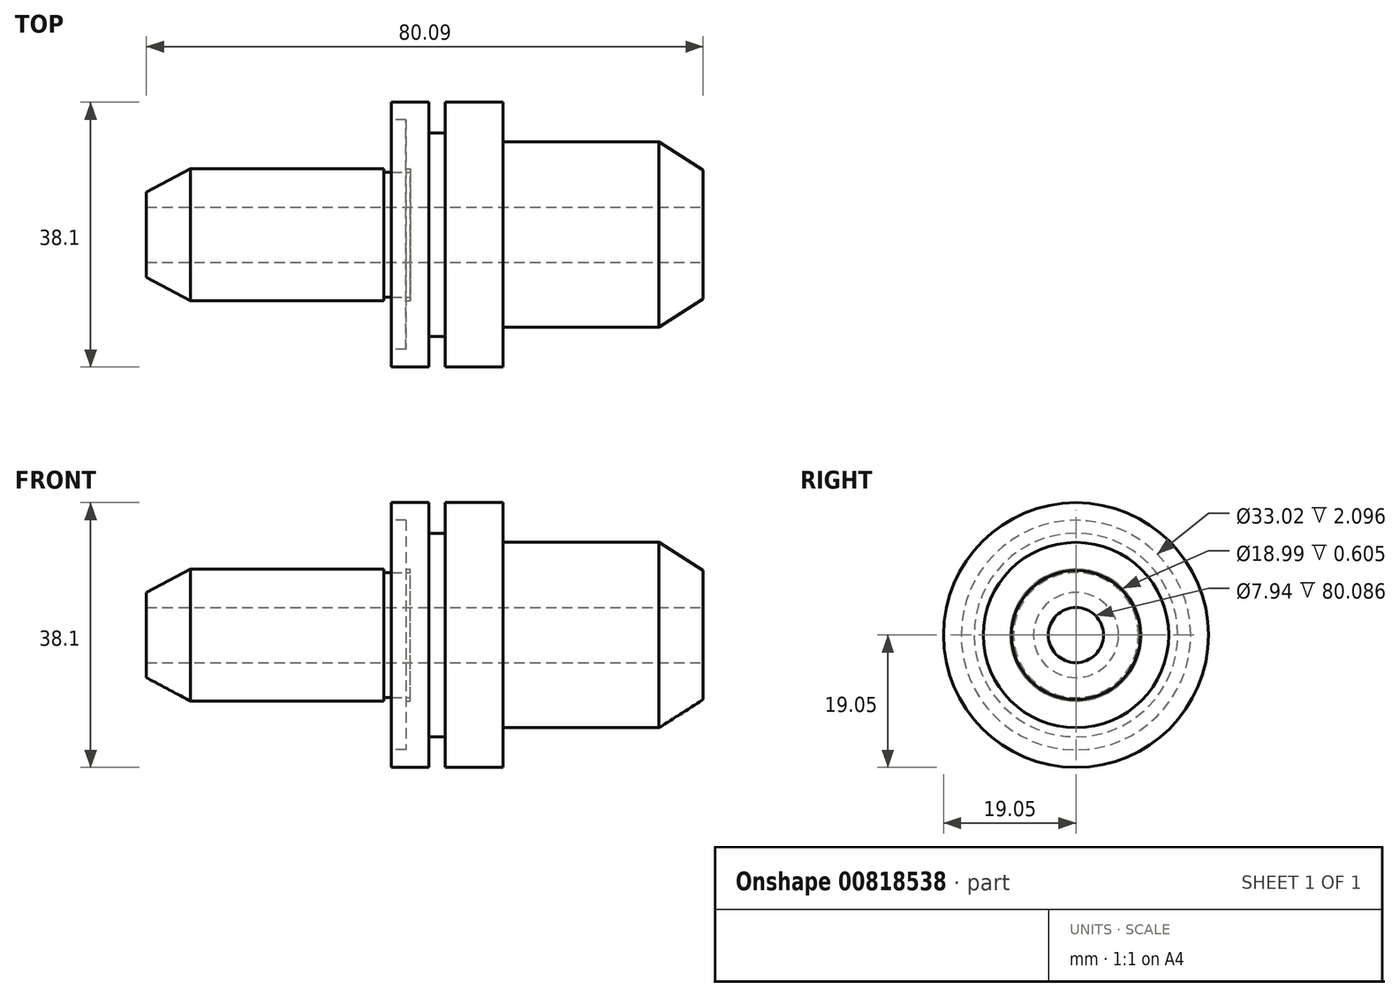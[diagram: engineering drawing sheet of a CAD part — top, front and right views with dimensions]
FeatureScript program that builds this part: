
annotation { "Feature Type Name" : "Feature", "Feature Type Description" : "" }
export const myFeature = defineFeature(function(context is Context, id is Id, definition is map)
    precondition{}
    {
        {
            var Q0;
            Q0=qCreatedBy(makeId("Right.planeOp"),FACE);
            var sketch = newSketch(context, id + "F0", { "sketchPlane" : qUnion([Q0])});
            skCircle(sketch, "E0", {"center": v(0, 0) * mm, "radius": 9.5 * mm});
            skSolve(sketch);
        }
        {
            var Q0;
            Q0 = qSketchRegion(id + "F0", true);
            extrude(context, id + "F1", {"entities" : qUnion([Q0]), "depth" : 35.24 * mm, "offsetDistance" : 25.4 * mm});
        }
        {
            var Q0;
            Q0=makeQuery(id+"F1.opExtrude","CAP_FACE",FACE,{"disambiguationData":[OSD([sQuery(id+"F0.wireOp",EDGE,"E0")])],"isStart":false});
            var sketch = newSketch(context, id + "F2", { "sketchPlane" : qUnion([Q0])});
            skCircle(sketch, "E1", {"center": v(0, 0) * mm, "radius": 19.05 * mm});
            skSolve(sketch);
        }
        {
            var Q0;
            Q0 = qSketchRegion(id + "F2", true);
            extrude(context, id + "F3", {"entities" : qUnion([Q0]), "operationType" : NewBodyOperationType.ADD, "depth" : 16.08 * mm, "offsetDistance" : 25.4 * mm});
        }
        {
            var Q0;
            Q0=makeQuery(id+"F3.opExtrude","CAP_FACE",FACE,{"disambiguationData":[OSD([sQuery(id+"F2.wireOp",EDGE,"E1")])],"isStart":false});
            var sketch = newSketch(context, id + "F4", { "sketchPlane" : qUnion([Q0])});
            skCircle(sketch, "E2", {"center": v(0, 0) * mm, "radius": 13.34 * mm});
            skSolve(sketch);
        }
        {
            var Q0;
            Q0 = qSketchRegion(id + "F4", true);
            extrude(context, id + "F5", {"entities" : qUnion([Q0]), "operationType" : NewBodyOperationType.ADD, "depth" : 28.77 * mm, "offsetDistance" : 25.4 * mm});
        }
        {
            var Q0;
            Q0=makeQuery(id+"F5.opExtrude","CAP_FACE",FACE,{"disambiguationData":[OSD([sQuery(id+"F4.wireOp",EDGE,"E2")])],"isStart":false});
            var sketch = newSketch(context, id + "F6", { "sketchPlane" : qUnion([Q0])});
            skCircle(sketch, "E3", {"center": v(0, 0) * mm, "radius": 3.97 * mm});
            skSolve(sketch);
        }
        {
            var Q0;
            Q0 = qSketchRegion(id + "F6", true);
            extrude(context, id + "F7", {"entities" : qUnion([Q0]), "operationType" : NewBodyOperationType.REMOVE, "endBound" : BoundingType.UP_TO_NEXT, "oppositeDirection" : true, "depth" : 25.4 * mm, "offsetDistance" : 25.4 * mm});
        }
        {
            var Q0;
            Q0=makeQuery(id+"F3.opExtrude","CAP_FACE",FACE,{"disambiguationData":[OSD([sQuery(id+"F2.wireOp",EDGE,"E1")])],"isStart":true});
            var sketch = newSketch(context, id + "F8", { "sketchPlane" : qUnion([Q0])});
            skCircle(sketch, "E4.0", {"center": v(0, 0) * mm, "radius": 9.5 * mm});
            skCircle(sketch, "E5.0", {"center": v(0, 0) * mm, "radius": 16.51 * mm});
            skSolve(sketch);
        }
        {
            var Q0;
            Q0 = qSketchRegion(id + "F8", true);
            extrude(context, id + "F9", {"entities" : qUnion([Q0]), "operationType" : NewBodyOperationType.REMOVE, "oppositeDirection" : true, "depth" : 2.1 * mm, "offsetDistance" : 25.4 * mm});
        }
        {
            var Q0;
            Q0=qCreatedBy(makeId("Front.planeOp"),FACE);
            var sketch = newSketch(context, id + "F10", { "sketchPlane" : qUnion([Q0])});
            skLineSegment(sketch, "E6", {"start": v(34.13, 9.5) * mm, "end": v(37.94, 9.5) * mm});
            skLineSegment(sketch, "E7.bottom", {"start": v(37.94, 9.5) * mm, "end": v(34.13, 9.5) * mm});
            skLineSegment(sketch, "E7.top", {"start": v(37.94, 8.99) * mm, "end": v(34.13, 8.99) * mm});
            skLineSegment(sketch, "E7.left", {"start": v(37.94, 9.5) * mm, "end": v(37.94, 8.99) * mm});
            skLineSegment(sketch, "E7.right", {"start": v(34.13, 9.5) * mm, "end": v(34.13, 8.99) * mm});
            skLineSegment(sketch, "E8", {"start": v(0, 0) * mm, "end": v(87.51, 0) * mm, "construction": true});
            skSolve(sketch);
        }
        {
            var Q0;
            Q0 = qSketchRegion(id + "F10", true);
            var Q1;
            Q1=sQuery(id+"F10.wireOp",EDGE,"E8");
            revolve(context, id + "F11", {"operationType" : NewBodyOperationType.REMOVE, "surfaceOperationType" : NewSurfaceOperationType.NEW, "entities" : qUnion([Q0]), "axis" : qUnion([Q1]), "revolveType" : RevolveType.FULL, "oppositeDirection" : true});
        }
        {
            var Q0;
            Q0=qCreatedBy(makeId("Front.planeOp"),FACE);
            var sketch = newSketch(context, id + "F12", { "sketchPlane" : qUnion([Q0])});
            skLineSegment(sketch, "E9", {"start": v(40.64, 19.05) * mm, "end": v(42.99, 19.05) * mm});
            skLineSegment(sketch, "E10.top", {"start": v(40.64, 14.64) * mm, "end": v(42.99, 14.64) * mm});
            skLineSegment(sketch, "E10.left", {"start": v(40.64, 19.05) * mm, "end": v(40.64, 14.64) * mm});
            skLineSegment(sketch, "E10.right", {"start": v(42.99, 19.05) * mm, "end": v(42.99, 14.64) * mm});
            skLineSegment(sketch, "E11", {"start": v(0, 0) * mm, "end": v(85.99, 0) * mm, "construction": true});
            skSolve(sketch);
        }
        {
            var Q0;
            Q0 = qSketchRegion(id + "F12", true);
            var Q1;
            Q1=sQuery(id+"F12.wireOp",EDGE,"E11");
            revolve(context, id + "F13", {"operationType" : NewBodyOperationType.REMOVE, "surfaceOperationType" : NewSurfaceOperationType.NEW, "entities" : qUnion([Q0]), "axis" : qUnion([Q1]), "revolveType" : RevolveType.FULL, "oppositeDirection" : true});
        }
        {
            var Q0;
            Q0=qCreatedBy(makeId("Front.planeOp"),FACE);
            var sketch = newSketch(context, id + "F14", { "sketchPlane" : qUnion([Q0])});
            skLineSegment(sketch, "E12", {"start": v(0, 9.5) * mm, "end": v(6.35, 9.5) * mm});
            skLineSegment(sketch, "E13", {"start": v(73.74, 13.34) * mm, "end": v(80.09, 13.34) * mm});
            skLineSegment(sketch, "E14", {"start": v(0, 9.5) * mm, "end": v(0, 6.13) * mm});
            skLineSegment(sketch, "E15", {"start": v(0, 6.13) * mm, "end": v(6.35, 9.5) * mm});
            skLineSegment(sketch, "E16", {"start": v(80.09, 13.34) * mm, "end": v(80.09, 9.27) * mm});
            skLineSegment(sketch, "E17", {"start": v(80.09, 9.27) * mm, "end": v(73.74, 13.33) * mm});
            skLineSegment(sketch, "E18", {"start": v(0, 0) * mm, "end": v(83.47, 0) * mm, "construction": true});
            skSolve(sketch);
        }
        {
            var Q0;
            Q0 = qSketchRegion(id + "F14", true);
            var Q1;
            Q1=sQuery(id+"F14.wireOp",EDGE,"E18");
            revolve(context, id + "F15", {"operationType" : NewBodyOperationType.REMOVE, "surfaceOperationType" : NewSurfaceOperationType.NEW, "entities" : qUnion([Q0]), "axis" : qUnion([Q1]), "revolveType" : RevolveType.FULL, "oppositeDirection" : true});
        }
    });
